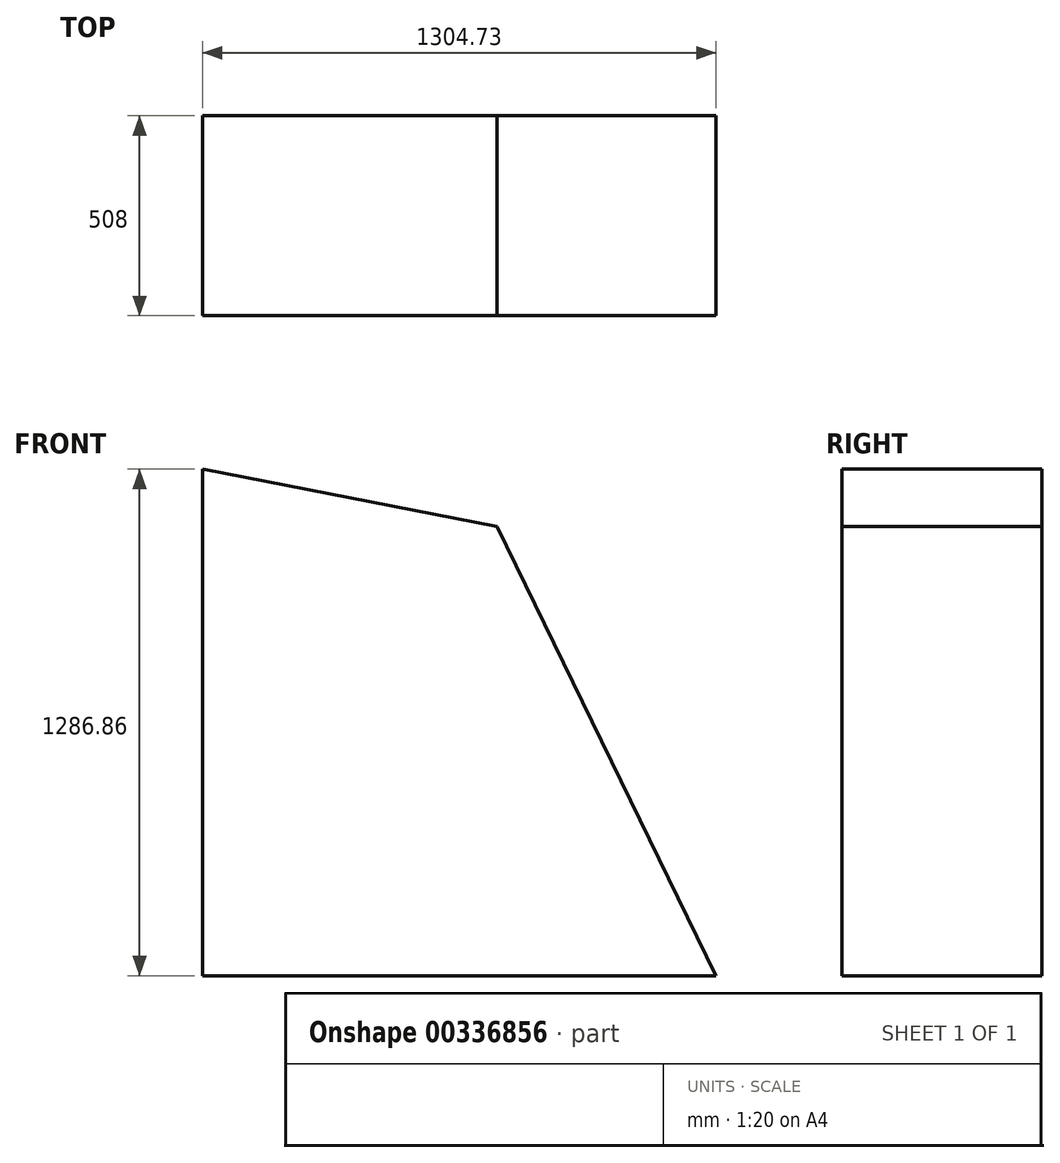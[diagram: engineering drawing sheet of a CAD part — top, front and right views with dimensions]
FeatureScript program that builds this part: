
annotation { "Feature Type Name" : "Feature", "Feature Type Description" : "" }
export const myFeature = defineFeature(function(context is Context, id is Id, definition is map)
    precondition{}
    {
        {
            var Q0;
            Q0=qCreatedBy(makeId("Front.planeOp"),FACE);
            var sketch = newSketch(context, id + "F0", { "sketchPlane" : qUnion([Q0])});
            skLineSegment(sketch, "E0", {"start": v(0, 0) * mm, "end": v(1304.73, 0) * mm});
            skLineSegment(sketch, "E1", {"start": v(1304.73, 0) * mm, "end": v(748, 1141.47) * mm});
            skLineSegment(sketch, "E2", {"start": v(748, 1141.47) * mm, "end": v(0, 1286.86) * mm});
            skLineSegment(sketch, "E3", {"start": v(0, 1286.86) * mm, "end": v(0, 0) * mm});
            skSolve(sketch);
        }
        {
            var Q0;
            Q0=makeQuery(id+"F0.imprint","IMPRINT",FACE,{"disambiguationData":[TD([[makeQuery(id+"F0.imprint","IMPRINT",EDGE,{"derivedFrom":sQuery(id+"F0.wireOp",EDGE,"E0")}),1.0]])]});
            extrude(context, id + "F1", {"entities" : qUnion([Q0]), "depth" : 508 * mm});
        }
    });
